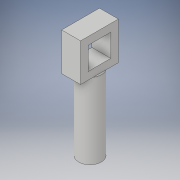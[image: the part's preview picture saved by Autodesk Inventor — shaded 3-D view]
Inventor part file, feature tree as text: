
AUTODESK INVENTOR PART (.ipt)
format: ipt  version: 2019 (Build 230136000, 136)  size: 116,736 bytes
history: native  units: mm
features: extrude x2, sketch x2
ambient origin geometry x8: Origin, YZ Plane, XZ Plane, XY Plane, X Axis, Y Axis, Z Axis, Center Point
bodies: Solid1 (feature_tree)
feature tree (4):
  extrude  "Extrusion1"  Depth=6.0mm
  extrude  "Extrusion2"  Depth=10.0mm
  sketch  "Sketch1"  dims[d0=6.0mm d1=6.0mm]
  sketch  "Sketch2"  dims[d2=2.0mm d3=10.0mm d4=10.0mm d5=2.0mm d6=5.0mm d7=0.0mm d8=6.0mm d9=5.0mm d10=2.5mm d11=20.0mm d12=0.0mm]
